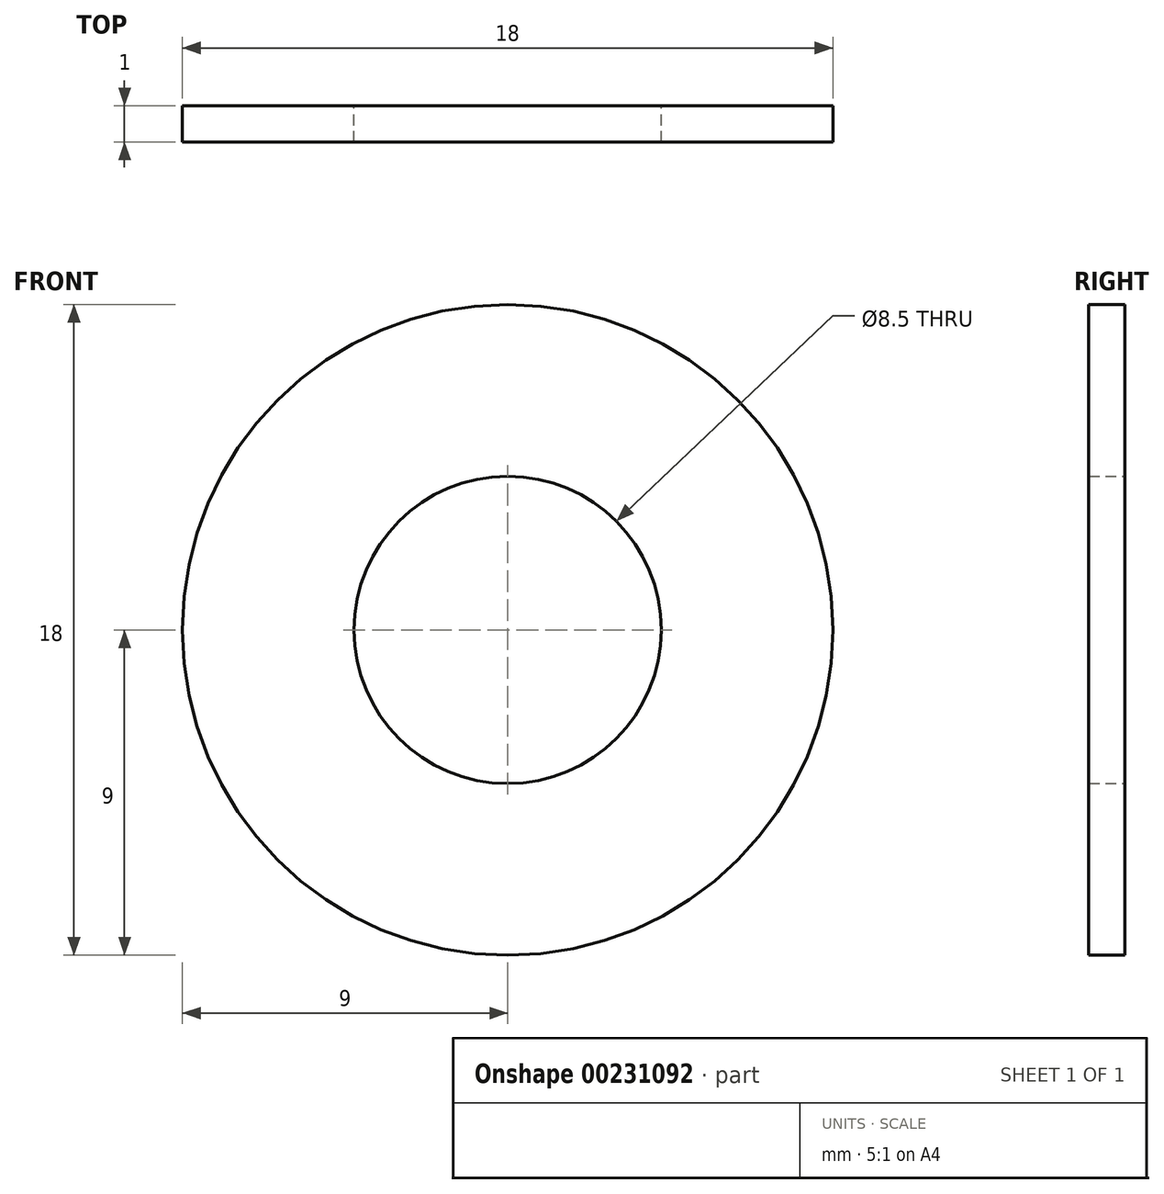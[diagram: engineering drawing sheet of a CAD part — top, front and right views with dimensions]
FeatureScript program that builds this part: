
annotation { "Feature Type Name" : "Feature", "Feature Type Description" : "" }
export const myFeature = defineFeature(function(context is Context, id is Id, definition is map)
    precondition{}
    {
        {
            var Q0;
            Q0=qCreatedBy(makeId("Front.planeOp"),FACE);
            var sketch = newSketch(context, id + "F0", { "sketchPlane" : qUnion([Q0])});
            skCircle(sketch, "E0", {"center": v(0, 0) * mm, "radius": 9 * mm});
            skCircle(sketch, "E1", {"center": v(0, 0) * mm, "radius": 4.25 * mm});
            skSolve(sketch);
        }
        {
            var Q0;
            Q0=makeQuery(id+"F0.imprint","IMPRINT",FACE,{"disambiguationData":[TD([[makeQuery(id+"F0.imprint","IMPRINT",EDGE,{"derivedFrom":sQuery(id+"F0.wireOp",EDGE,"E0")}),1.0]])]});
            extrude(context, id + "F1", {"entities" : qUnion([Q0]), "depth" : 1 * mm});
        }
    });
